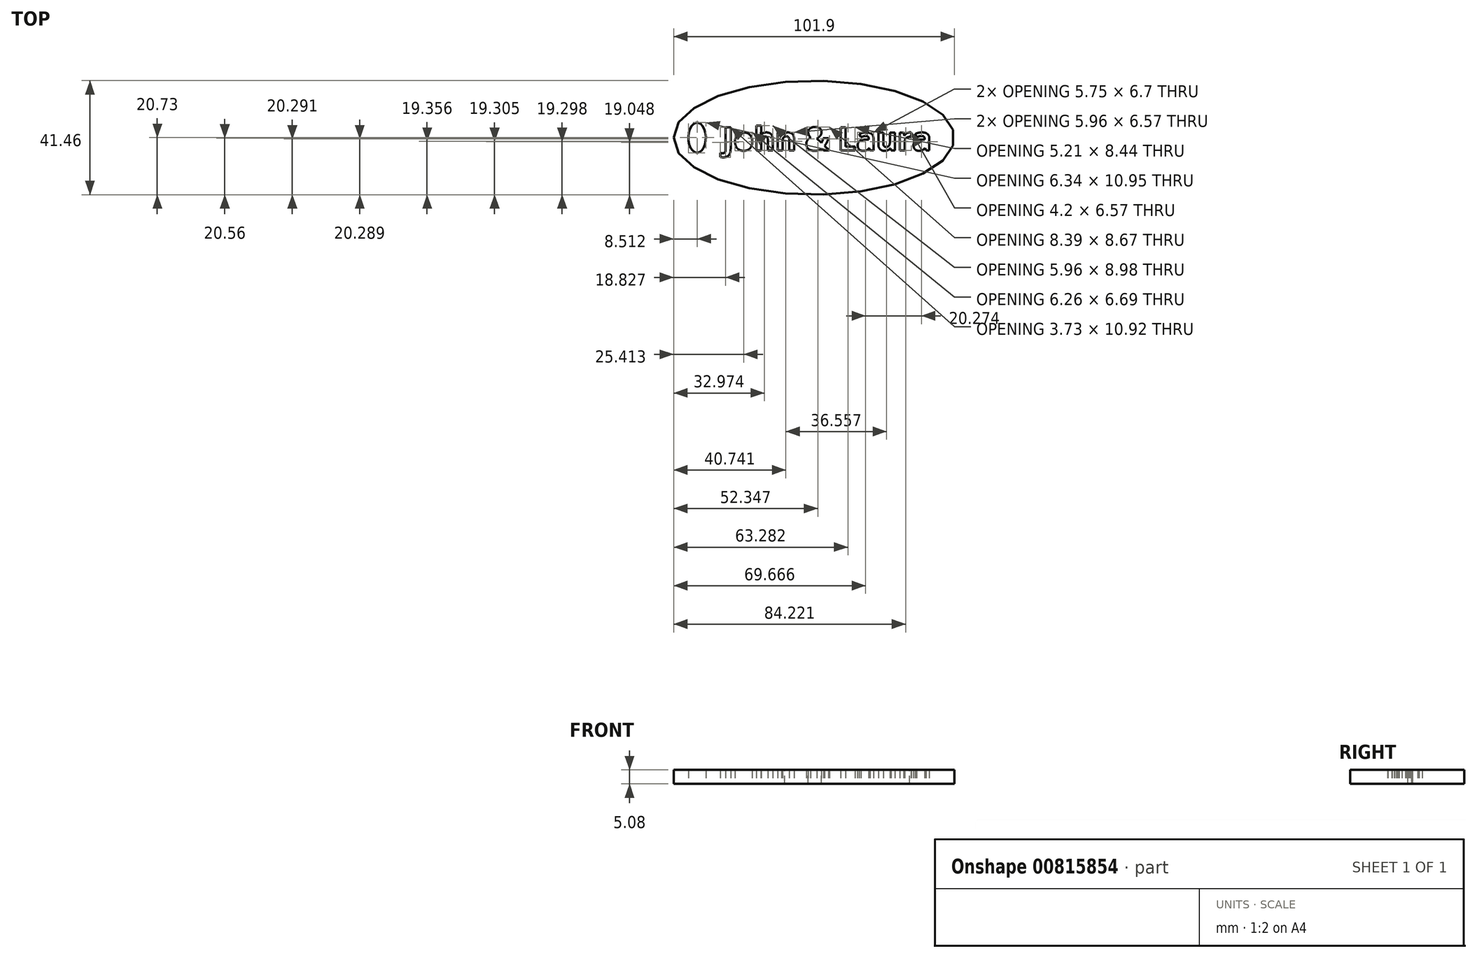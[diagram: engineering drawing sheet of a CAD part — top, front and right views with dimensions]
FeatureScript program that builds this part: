
annotation { "Feature Type Name" : "Feature", "Feature Type Description" : "" }
export const myFeature = defineFeature(function(context is Context, id is Id, definition is map)
    precondition{}
    {
        {
            var Q0;
            Q0=qCreatedBy(makeId("Top.planeOp"),FACE);
            var sketch = newSketch(context, id + "F0", { "sketchPlane" : qUnion([Q0])});
            skText(sketch, "E0", { "text": "John & Laura", "fontName": "NotoSans-Bold.ttf"});
            skEllipse(sketch, "E1", {"center": v(0, 0) * mm, "majorRadius": 50.95 * mm, "minorRadius": 20.73 * mm, "majorAxis": v(-1, 0)});
            skEllipse(sketch, "E2", {"center": v(-42.44, 0) * mm, "majorRadius": 5.47 * mm, "minorRadius": 3.17 * mm, "majorAxis": v(0, -1)});
            const initialGuessF0  = {"E0": [-0.03311, -0.00466, 1, 0, 0.00851]};
            skSetInitialGuess(sketch, initialGuessF0);
            skSolve(sketch);
        }
        {
            var Q0;
            Q0=makeQuery(id+"F0.imprint","IMPRINT",FACE,{"disambiguationData":[TD([[makeQuery(id+"F0.imprint","IMPRINT",EDGE,{"derivedFrom":sQuery(id+"F0.wireOp",EDGE,"E0.sketch_text.stroke-0")}),1.0]])]});
            extrude(context, id + "F1", {"entities" : qUnion([Q0]), "depth" : 5.08 * mm, "offsetDistance" : 25.4 * mm});
        }
    });
